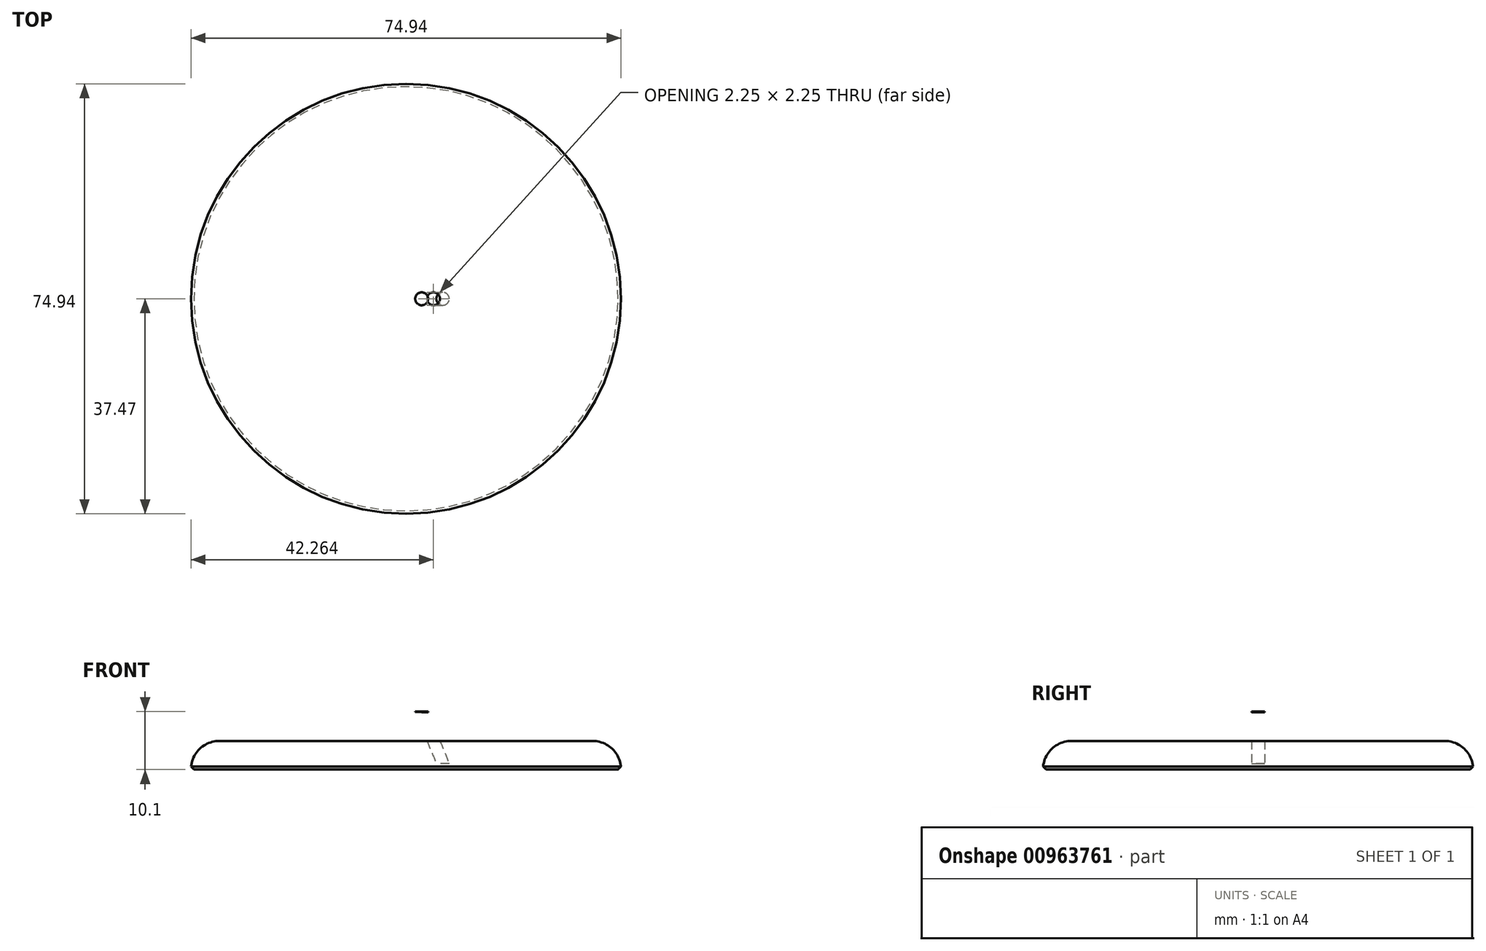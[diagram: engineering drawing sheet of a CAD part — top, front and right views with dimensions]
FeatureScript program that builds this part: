
annotation { "Feature Type Name" : "Feature", "Feature Type Description" : "" }
export const myFeature = defineFeature(function(context is Context, id is Id, definition is map)
    precondition{}
    {
        {
            var Q0;
            Q0=qCreatedBy(makeId("Top.planeOp"),FACE);
            var sketch = newSketch(context, id + "F0", { "sketchPlane" : qUnion([Q0])});
            skCircle(sketch, "E0", {"center": v(0, 0) * mm, "radius": 37.5 * mm});
            skSolve(sketch);
        }
        {
            var Q0;
            Q0=qSketchRegion(id+"F0",true);
            extrude(context, id + "F1", {"entities" : qUnion([Q0]), "depth" : 5 * mm, "offsetDistance" : 25 * mm});
        }
        {
            var Q0;
            Q0=makeQuery(id+"F1.opExtrude","CAP_EDGE",EDGE,{"disambiguationData":[OSD([sQuery(id+"F0.wireOp",EDGE,"E0")])],"isStart":false});
            fillet(context, id + "F2", {"entities" : qUnion([Q0]), "radius" : 5 * mm, "tangentPropagation" : true, "allowEdgeOverflow" : false});
        }
        {
            var Q0;
            {var subQ0=sQuery(id+"F0.wireOp",EDGE,"E0");Q0=makeQuery(id+"F2.opFillet","BLEND_EDGE",EDGE,{"blendedFrom":[makeQuery(id+"F1.opExtrude","CAP_EDGE",EDGE,{"disambiguationData":[OSD([subQ0])],"isStart":false}),makeQuery(id+"F1.opExtrude","CAP_FACE",FACE,{"disambiguationData":[OSD([subQ0])],"isStart":true})],"blendedInto":[makeQuery(id+"F1.opExtrude","CAP_FACE",FACE,{"disambiguationData":[OSD([subQ0])],"isStart":true})]});}
            chamfer(context, id + "F3", {"entities" : qUnion([Q0]), "width" : .5 * mm, "tangentPropagation" : true});
        }
        {
            var Q0;
            Q0=qCreatedBy(makeId("Top.planeOp"),FACE);
            cPlane(context, id + "F4", {"entities" : qUnion([Q0]), "cplaneType" : CPlaneType.OFFSET, "offset" : 10 * mm, "width" : 150 * mm, "height" : 150 * mm});
        }
        {
            var Q0;
            Q0=qCreatedBy(id+"F4.planeOp",FACE);
            var sketch = newSketch(context, id + "F5", { "sketchPlane" : qUnion([Q0])});
            skCircle(sketch, "E1", {"center": v(2.73, 0) * mm, "radius": 1.13 * mm});
            skSolve(sketch);
        }
        {
            var Q0;
            Q0=qCreatedBy(makeId("Front.planeOp"),FACE);
            var sketch = newSketch(context, id + "F6", { "sketchPlane" : qUnion([Q0])});
            skLineSegment(sketch, "E2", {"start": v(1.83, 10.05) * mm, "end": v(5.53, 1.06) * mm});
            skSolve(sketch);
        }
        {
            var Q0;
            Q0=makeQuery(id+"F5.imprint","IMPRINT",FACE,{"disambiguationData":[TD([[makeQuery(id+"F5.imprint","IMPRINT",EDGE,{"derivedFrom":sQuery(id+"F5.wireOp",EDGE,"E1")}),1.0]])]});
            extrude(context, id + "F7", {"entities" : qUnion([Q0]), "depth" : .1 * mm, "offsetDistance" : 25 * mm});
        }
        {
            var Q0;
            Q0=makeQuery(id+"F7.opExtrude","CAP_FACE",FACE,{"disambiguationData":[OSD([sQuery(id+"F5.wireOp",EDGE,"E1")])],"isStart":true});
            var Q1;
            Q1=makeQuery(id+"F7.opExtrude","CAP_EDGE",EDGE,{"disambiguationData":[OSD([sQuery(id+"F5.wireOp",EDGE,"E1")])],"isStart":true});
            var Q2;
            Q2=sQuery(id+"F6.wireOp",EDGE,"E2");
            sweep(context, id + "F8", {"operationType" : NewBodyOperationType.REMOVE, "profiles" : qUnion([Q0]), "surfaceOperationType" : NewSurfaceOperationType.ADD, "surfaceProfiles" : qUnion([Q1]), "path" : qUnion([Q2])});
        }
        {
            var Q0;
            Q0=makeQuery(id+"F1.opExtrude","SWEPT_BODY",BODY,{"disambiguationData":[OSD([sQuery(id+"F0.wireOp",EDGE,"E0")])]});
            transform(context, id + "F9", {"entities" : qUnion([Q0]), "transformType" : TransformType.TRANSLATION_3D, "dx" : 0 * mm, "dy" : 0 * mm, "dz" : 0 * mm, "makeCopy" : true});
        }
    });
